FCSTD DOCUMENT  (FreeCAD 0.21R33694 (Git))
Label: EPD
License: All rights reserved
LicenseURL: http://en.wikipedia.org/wiki/All_rights_reserved
objects: Sketcher::SketchObject×1, PartDesign::Body×1
note: 2 computed .brp shape members not serialized (recipe doc carries the construction recipe); baked Part::Feature solids carry a one-line shape summary decoded from their .brp

FEATURE [Sketcher::SketchObject] Sketch
  FullyConstrained = true
  MapMode = 5
  Support = -> [XY_Plane]
  sketch-geometry (8):
    g0: LineSegment StartX=-15.9 StartY=18.66 StartZ=0 EndX=15.9 EndY=18.66 EndZ=0
    g1: LineSegment StartX=15.9 StartY=18.66 StartZ=0 EndX=15.9 EndY=-18.66 EndZ=0
    g2: LineSegment StartX=15.9 StartY=-18.66 StartZ=0 EndX=-15.9 EndY=-18.66 EndZ=0
    g3: LineSegment StartX=-15.9 StartY=-18.66 StartZ=0 EndX=-15.9 EndY=18.66 EndZ=0
    g4: LineSegment StartX=-13.5 StartY=16.26 StartZ=0 EndX=13.5 EndY=16.26 EndZ=0
    g5: LineSegment StartX=13.5 StartY=16.26 StartZ=0 EndX=13.5 EndY=-10.74 EndZ=0
    g6: LineSegment StartX=13.5 StartY=-10.74 StartZ=0 EndX=-13.5 EndY=-10.74 EndZ=0
    g7: LineSegment StartX=-13.5 StartY=-10.74 StartZ=0 EndX=-13.5 EndY=16.26 EndZ=0
  constraints (21):
    c: Coincident(g0,g1)
    c: Coincident(g1,g2)
    c: Coincident(g2,g3)
    c: Coincident(g3,g0)
    c: Horizontal(g2)
    c: Vertical(g1)
    c: Distance(g0) = 31.8
    c: Distance(g3) = 37.32
    c: Symmetric(g0,g0,g-2)
    c: Coincident(g4,g5)
    c: Coincident(g5,g6)
    c: Coincident(g6,g7)
    c: Coincident(g7,g4)
    c: Vertical(g5)
    c: Vertical(g7)
    c: Symmetric(g4,g4,g-2)
    c: Distance(g4) = 27
    c: Distance(g7) = 27
    c: Horizontal(g6)
    c: Distance(g4,g0) = 2.4
    c: Symmetric(g0,g2,g-1)
FEATURE [PartDesign::Body] Body
  Group = -> [Sketch]
  Origin = -> Origin
